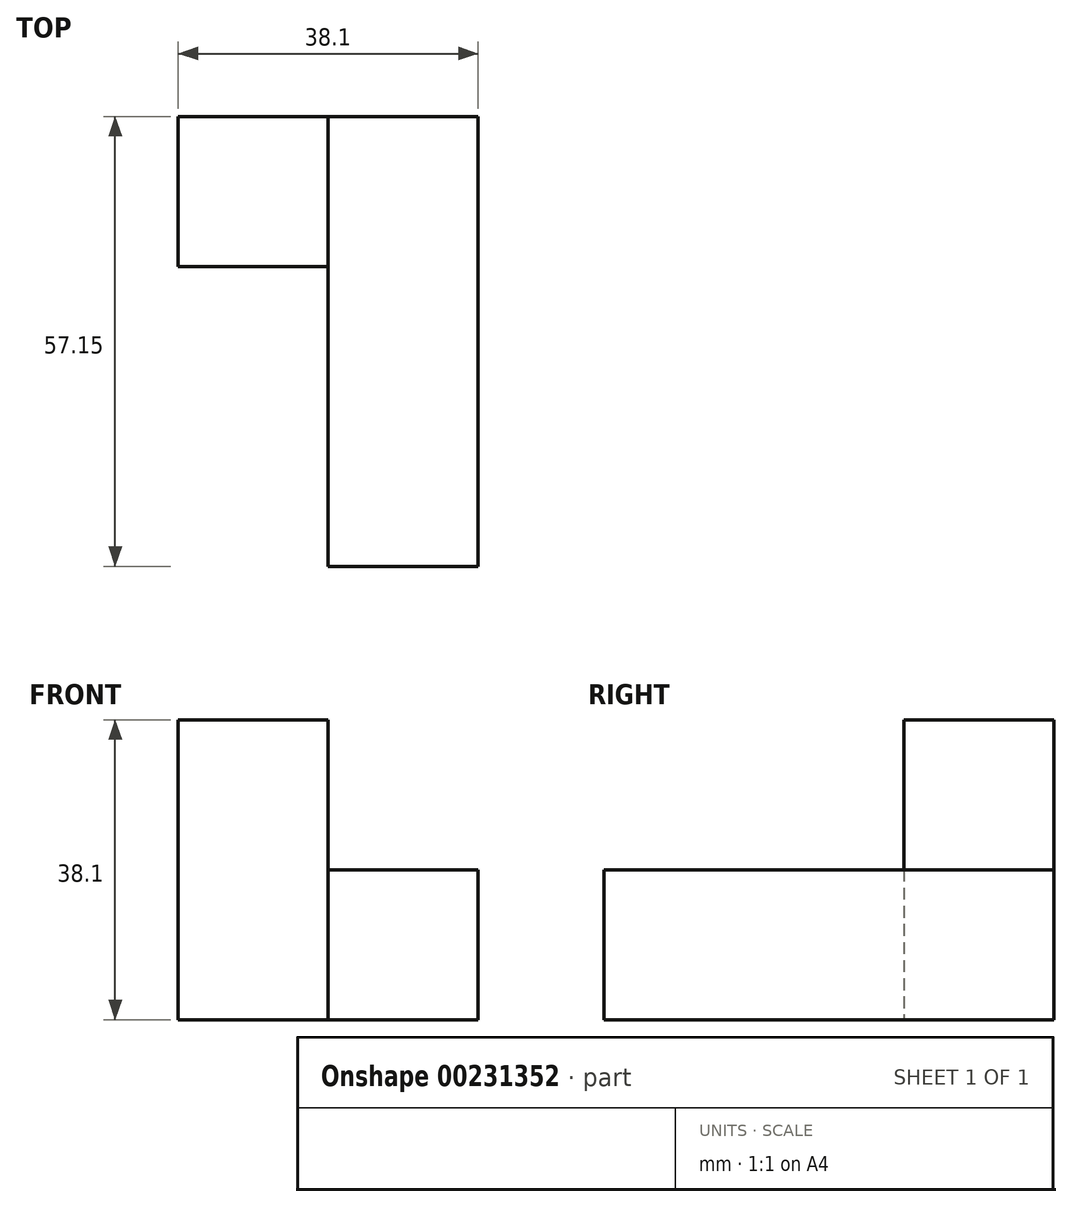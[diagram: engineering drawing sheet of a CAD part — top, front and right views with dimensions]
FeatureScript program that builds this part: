
annotation { "Feature Type Name" : "Feature", "Feature Type Description" : "" }
export const myFeature = defineFeature(function(context is Context, id is Id, definition is map)
    precondition{}
    {
        {
            var Q0;
            Q0=qCreatedBy(makeId("Front.planeOp"),FACE);
            var sketch = newSketch(context, id + "F0", { "sketchPlane" : qUnion([Q0])});
            skLineSegment(sketch, "E0.bottom", {"start": v(0, 19.05) * mm, "end": v(-19.05, 19.05) * mm});
            skLineSegment(sketch, "E0.top", {"start": v(0, 0) * mm, "end": v(-19.05, 0) * mm});
            skLineSegment(sketch, "E0.left", {"start": v(0, 19.05) * mm, "end": v(0, 0) * mm});
            skLineSegment(sketch, "E0.right", {"start": v(-19.05, 19.05) * mm, "end": v(-19.05, 0) * mm});
            skLineSegment(sketch, "E1.bottom", {"start": v(-19.05, 19.05) * mm, "end": v(-38.1, 19.05) * mm});
            skLineSegment(sketch, "E1.top", {"start": v(-19.05, 0) * mm, "end": v(-38.1, 0) * mm});
            skLineSegment(sketch, "E1.right", {"start": v(-38.1, 19.05) * mm, "end": v(-38.1, 0) * mm});
            skLineSegment(sketch, "E2.bottom", {"start": v(-38.1, 19.05) * mm, "end": v(-19.05, 19.05) * mm});
            skLineSegment(sketch, "E2.top", {"start": v(-38.1, 38.1) * mm, "end": v(-19.05, 38.1) * mm});
            skLineSegment(sketch, "E2.left", {"start": v(-38.1, 19.05) * mm, "end": v(-38.1, 38.1) * mm});
            skLineSegment(sketch, "E2.right", {"start": v(-19.05, 19.05) * mm, "end": v(-19.05, 38.1) * mm});
            skSolve(sketch);
        }
        {
            var Q0;
            Q0 = qSketchRegion(id + "F0", true);
            extrude(context, id + "F1", {"entities" : qUnion([Q0]), "depth" : 19.05 * mm});
        }
        {
            var Q0;
            Q0=makeQuery(id+"F1.opExtrude","CAP_FACE",FACE,{"disambiguationData":[OSD([sQuery(id+"F0.wireOp",EDGE,"E0.bottom"),sQuery(id+"F0.wireOp",EDGE,"E0.top"),sQuery(id+"F0.wireOp",EDGE,"E0.left"),sQuery(id+"F0.wireOp",EDGE,"E1.top"),sQuery(id+"F0.wireOp",EDGE,"E1.right"),sQuery(id+"F0.wireOp",EDGE,"E2.top"),sQuery(id+"F0.wireOp",EDGE,"E2.left"),sQuery(id+"F0.wireOp",EDGE,"E2.right")])],"isStart":false});
            var sketch = newSketch(context, id + "F2", { "sketchPlane" : qUnion([Q0])});
            skLineSegment(sketch, "E3.bottom", {"start": v(0, 19.05) * mm, "end": v(-19.05, 19.05) * mm});
            skLineSegment(sketch, "E3.top", {"start": v(0, 0) * mm, "end": v(-19.05, 0) * mm});
            skLineSegment(sketch, "E3.left", {"start": v(0, 19.05) * mm, "end": v(0, 0) * mm});
            skLineSegment(sketch, "E3.right", {"start": v(-19.05, 19.05) * mm, "end": v(-19.05, 0) * mm});
            skSolve(sketch);
        }
        {
            var Q0;
            Q0 = qSketchRegion(id + "F2", true);
            extrude(context, id + "F3", {"entities" : qUnion([Q0]), "operationType" : NewBodyOperationType.ADD, "depth" : 38.1 * mm});
        }
    });
